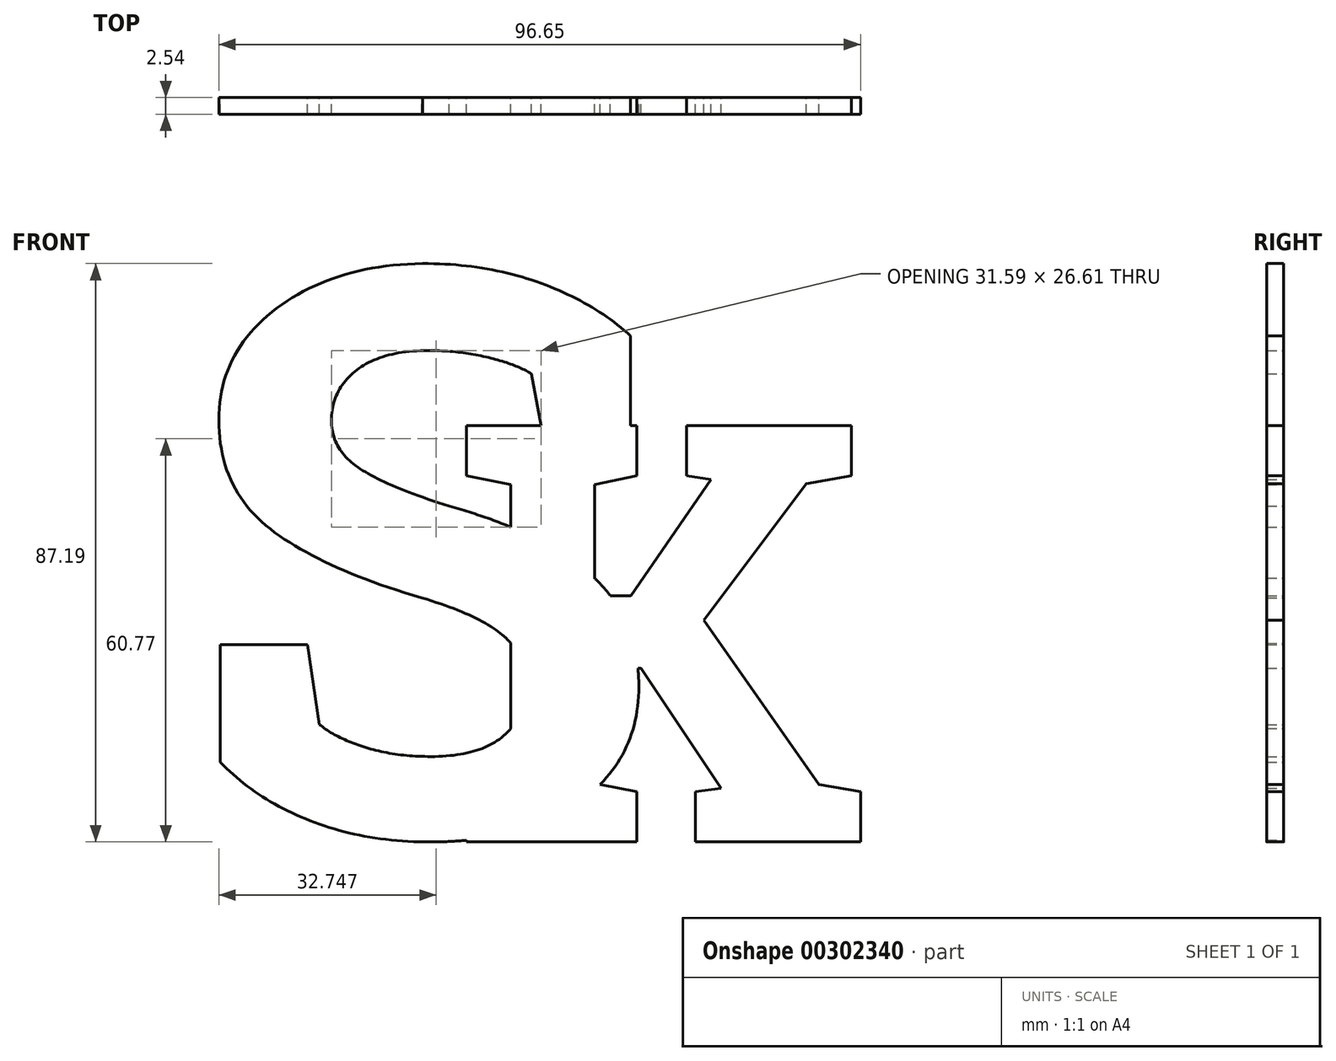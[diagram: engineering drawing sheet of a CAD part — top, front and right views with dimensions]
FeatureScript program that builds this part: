
annotation { "Feature Type Name" : "Feature", "Feature Type Description" : "" }
export const myFeature = defineFeature(function(context is Context, id is Id, definition is map)
    precondition{}
    {
        {
            var Q0;
            Q0=qCreatedBy(makeId("Front.planeOp"),FACE);
            var sketch = newSketch(context, id + "F0", { "sketchPlane" : qUnion([Q0])});
            skText(sketch, "E0", { "text": "S", "fontName": "RobotoSlab-Bold.ttf"});
            const initialGuessF0  = {"E0": [-0.0381, -0.04164, 1, 0, 0.08587]};
            skSetInitialGuess(sketch, initialGuessF0);
            skSolve(sketch);
        }
        {
            var Q0;
            Q0=makeQuery(id+"F0.imprint","IMPRINT",FACE,{"disambiguationData":[TD([[makeQuery(id+"F0.imprint","IMPRINT",EDGE,{"derivedFrom":sQuery(id+"F0.wireOp",EDGE,"E0.sketch_text.stroke-0")}),-1.0]])]});
            extrude(context, id + "F1", {"entities" : qUnion([Q0]), "depth" : 2.54 * mm});
        }
        {
            var Q0;
            Q0=qCreatedBy(makeId("Front.planeOp"),FACE);
            var sketch = newSketch(context, id + "F2", { "sketchPlane" : qUnion([Q0])});
            skText(sketch, "E1", { "text": "K", "fontName": "RobotoSlab-Bold.ttf"});
            const initialGuessF2  = {"E1": [0.00244, -0.04286, 1, 0, 0.06355]};
            skSetInitialGuess(sketch, initialGuessF2);
            skSolve(sketch);
        }
        {
            var Q0;
            Q0 = qSketchRegion(id + "F2", true);
            extrude(context, id + "F3", {"entities" : qUnion([Q0]), "operationType" : NewBodyOperationType.ADD, "depth" : 2.54 * mm});
        }
    });
